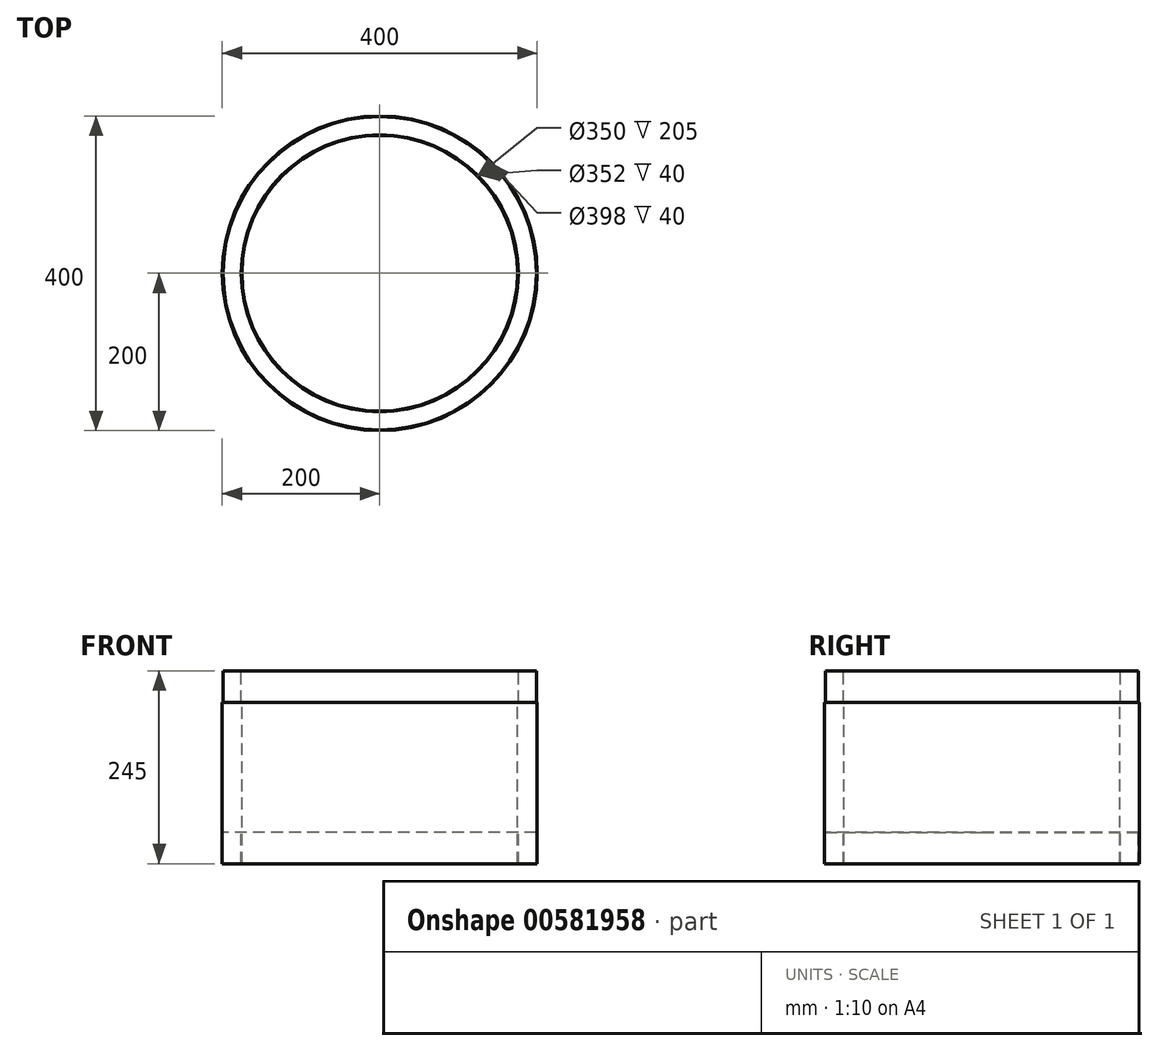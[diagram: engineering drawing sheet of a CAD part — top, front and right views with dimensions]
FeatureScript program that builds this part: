
annotation { "Feature Type Name" : "Feature", "Feature Type Description" : "" }
export const myFeature = defineFeature(function(context is Context, id is Id, definition is map)
    precondition{}
    {
        {
            var Q0;
            Q0=qCreatedBy(makeId("Front.planeOp"),FACE);
            var sketch = newSketch(context, id + "F0", { "sketchPlane" : qUnion([Q0])});
            skLineSegment(sketch, "E0", {"start": v(0, 345.75) * mm, "end": v(0, -558.03) * mm, "construction": true});
            skLineSegment(sketch, "E1", {"start": v(-175, -518.84) * mm, "end": v(-175, -313.84) * mm});
            skLineSegment(sketch, "E2", {"start": v(-175, -313.84) * mm, "end": v(-176, -313.84) * mm});
            skLineSegment(sketch, "E3", {"start": v(-176, -313.84) * mm, "end": v(-176, -273.84) * mm});
            skLineSegment(sketch, "E4", {"start": v(-176, -273.84) * mm, "end": v(-199, -273.84) * mm});
            skLineSegment(sketch, "E5", {"start": v(-199, -273.84) * mm, "end": v(-199, -313.84) * mm});
            skLineSegment(sketch, "E6", {"start": v(-199, -313.84) * mm, "end": v(-200, -313.84) * mm});
            skLineSegment(sketch, "E7", {"start": v(-200, -313.84) * mm, "end": v(-200, -518.84) * mm});
            skLineSegment(sketch, "E8", {"start": v(-200, -518.84) * mm, "end": v(-199, -518.84) * mm});
            skLineSegment(sketch, "E9", {"start": v(-199, -518.84) * mm, "end": v(-199, -478.84) * mm});
            skLineSegment(sketch, "E10", {"start": v(-199, -478.84) * mm, "end": v(-176, -478.84) * mm});
            skLineSegment(sketch, "E11", {"start": v(-176, -478.84) * mm, "end": v(-176, -518.84) * mm});
            skLineSegment(sketch, "E12", {"start": v(-176, -518.84) * mm, "end": v(-175, -518.84) * mm});
            skSolve(sketch);
        }
        {
            var Q0;
            Q0=qSketchRegion(id+"F0",true);
            var Q1;
            Q1=sQuery(id+"F0.wireOp",EDGE,"E0");
            revolve(context, id + "F1", {"entities" : qUnion([Q0]), "axis" : qUnion([Q1]), "revolveType" : RevolveType.FULL});
        }
    });
